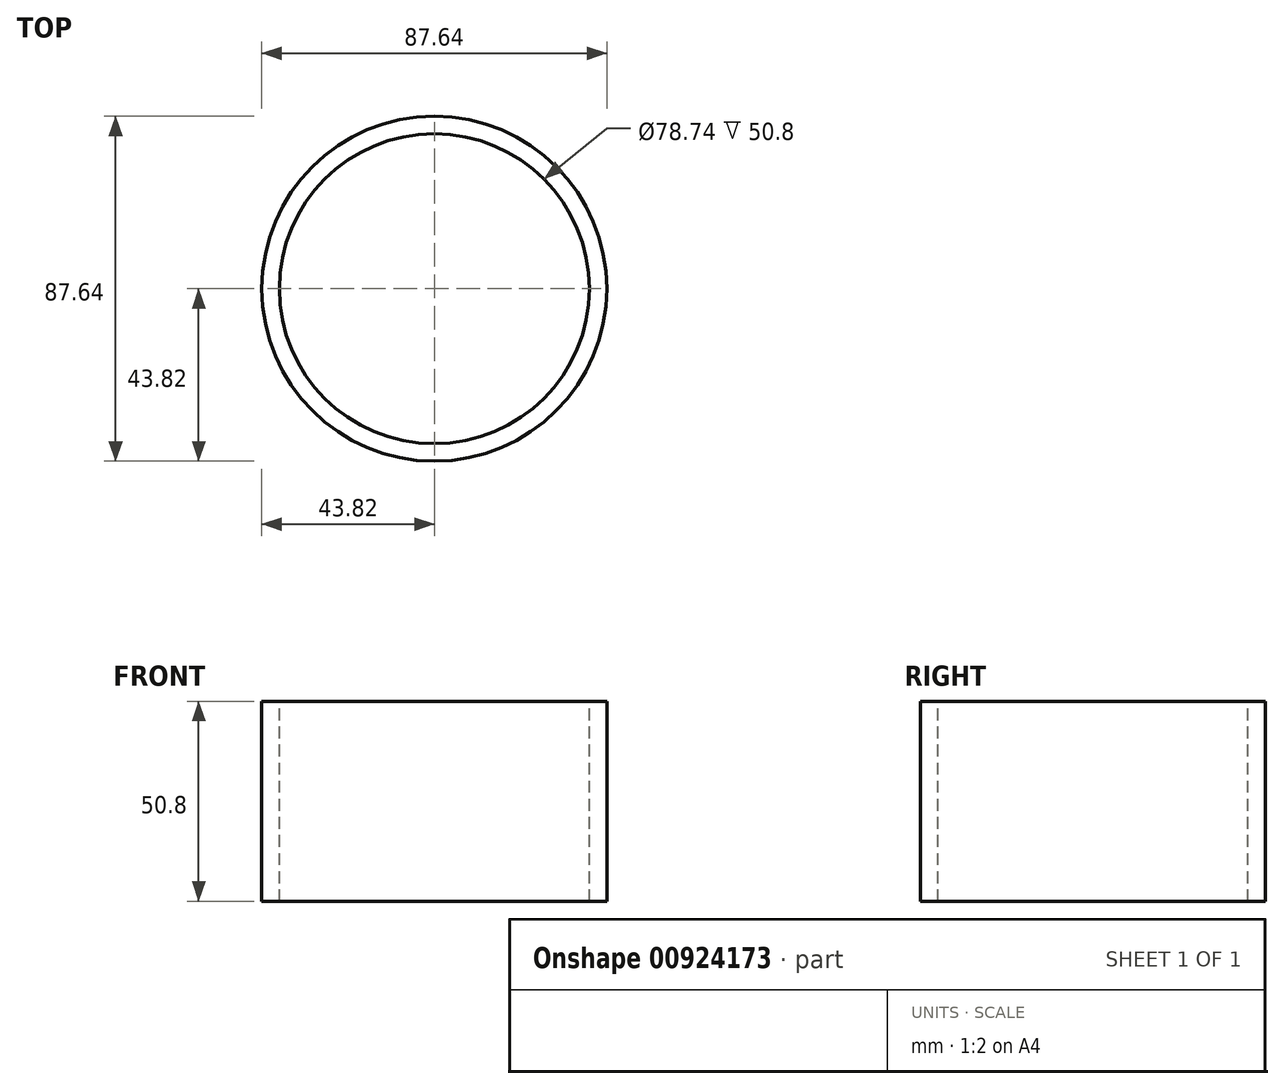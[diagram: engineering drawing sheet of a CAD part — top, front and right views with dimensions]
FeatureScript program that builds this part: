
annotation { "Feature Type Name" : "Feature", "Feature Type Description" : "" }
export const myFeature = defineFeature(function(context is Context, id is Id, definition is map)
    precondition{}
    {
        {
            var Q0;
            Q0=qCreatedBy(makeId("Top.planeOp"),FACE);
            var sketch = newSketch(context, id + "F0", { "sketchPlane" : qUnion([Q0])});
            skCircle(sketch, "E0", {"center": v(0, 0) * mm, "radius": 43.82 * mm});
            skCircle(sketch, "E1.0", {"center": v(0, 0) * mm, "radius": 39.37 * mm});
            skSolve(sketch);
        }
        {
            var Q0;
            Q0 = qSketchRegion(id + "F0", true);
            extrude(context, id + "F1", {"entities" : qUnion([Q0]), "oppositeDirection" : true, "depth" : 50.8 * mm, "offsetDistance" : 25.4 * mm});
        }
    });
